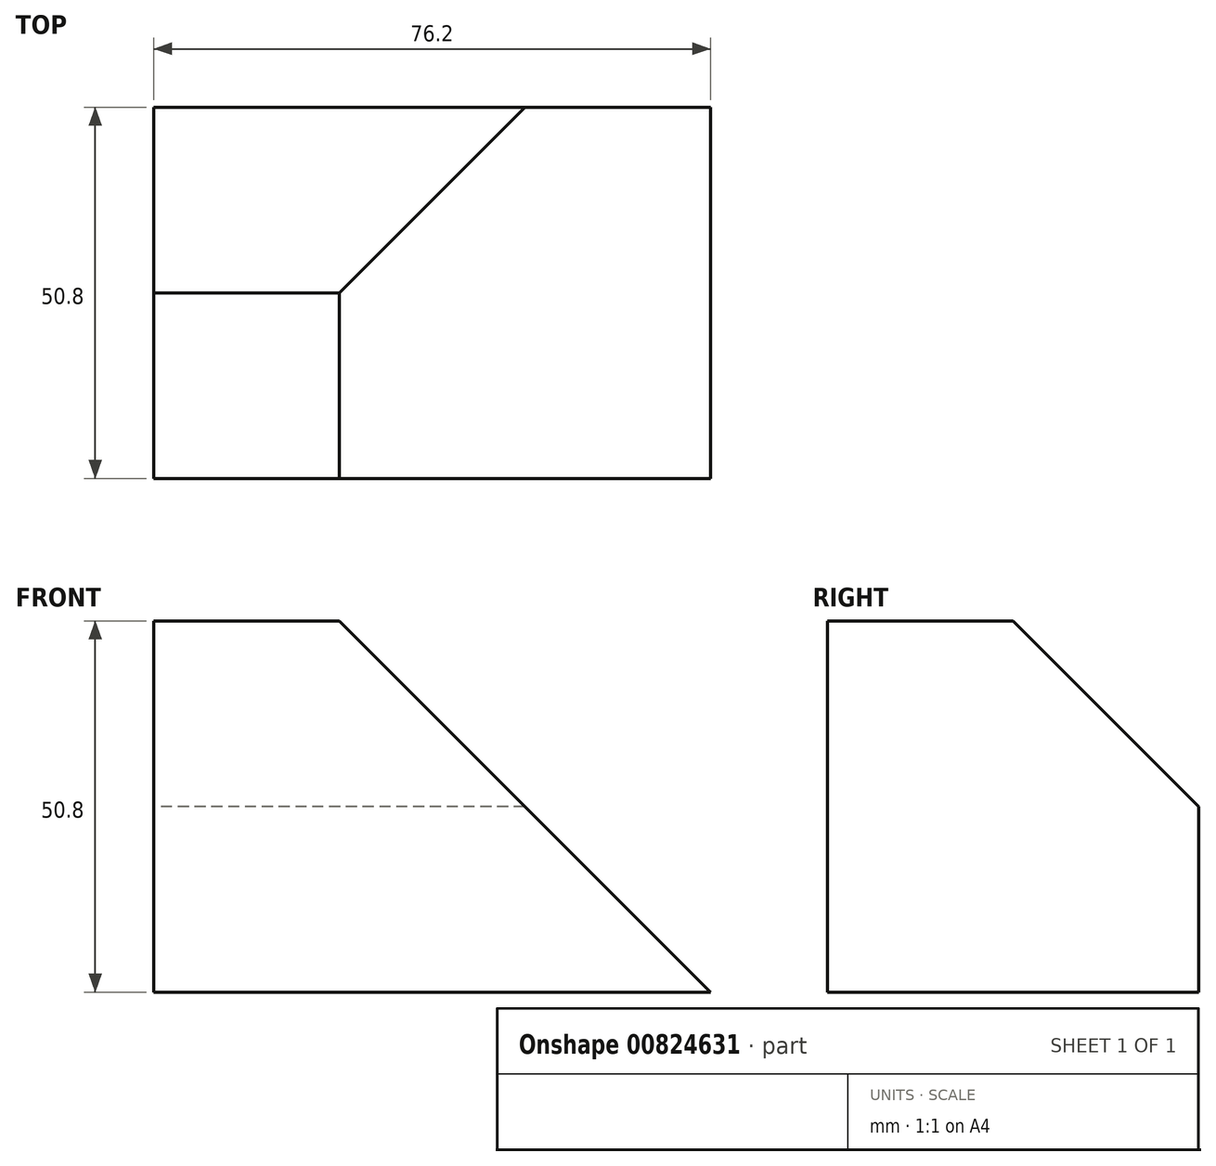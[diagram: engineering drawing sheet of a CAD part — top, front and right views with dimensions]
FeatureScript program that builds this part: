
annotation { "Feature Type Name" : "Feature", "Feature Type Description" : "" }
export const myFeature = defineFeature(function(context is Context, id is Id, definition is map)
    precondition{}
    {
        {
            var Q0;
            Q0=qCreatedBy(makeId("Front.planeOp"),FACE);
            var sketch = newSketch(context, id + "F0", { "sketchPlane" : qUnion([Q0])});
            skLineSegment(sketch, "E0", {"start": v(0, 0) * mm, "end": v(76.2, 0) * mm});
            skLineSegment(sketch, "E1", {"start": v(0, 0) * mm, "end": v(0, 25.4) * mm});
            skLineSegment(sketch, "E2", {"start": v(0, 25.4) * mm, "end": v(0, 50.8) * mm});
            skLineSegment(sketch, "E3", {"start": v(0, 50.8) * mm, "end": v(25.4, 50.8) * mm});
            skLineSegment(sketch, "E4", {"start": v(25.4, 50.8) * mm, "end": v(25.4, 25.4) * mm});
            skLineSegment(sketch, "E5", {"start": v(25.4, 25.4) * mm, "end": v(76.2, 0) * mm});
            skLineSegment(sketch, "E6", {"start": v(0, 25.4) * mm, "end": v(25.4, 25.4) * mm});
            skLineSegment(sketch, "E7", {"start": v(25.4, 50.8) * mm, "end": v(76.2, 0) * mm});
            skSolve(sketch);
        }
        {
            var Q0;
            Q0=makeQuery(id+"F0.imprint","IMPRINT",FACE,{"disambiguationData":[TD([[makeQuery(id+"F0.imprint","IMPRINT",EDGE,{"derivedFrom":sQuery(id+"F0.wireOp",EDGE,"E4")}),1.0]])]});
            var Q1;
            Q1=makeQuery(id+"F0.imprint","IMPRINT",FACE,{"disambiguationData":[TD([[makeQuery(id+"F0.imprint","IMPRINT",EDGE,{"derivedFrom":sQuery(id+"F0.wireOp",EDGE,"E2")}),-1.0]])]});
            var Q2;
            Q2=makeQuery(id+"F0.imprint","IMPRINT",FACE,{"disambiguationData":[TD([[makeQuery(id+"F0.imprint","IMPRINT",EDGE,{"derivedFrom":sQuery(id+"F0.wireOp",EDGE,"E0")}),1.0]])]});
            extrude(context, id + "F1", {"entities" : qUnion([Q0, Q1, Q2]), "depth" : 50.8 * mm, "offsetDistance" : 25.4 * mm});
        }
        {
            var Q0;
            Q0=makeQuery(id+"F1.opExtrude","SWEPT_FACE",FACE,{"disambiguationData":[OSD([sQuery(id+"F0.wireOp",EDGE,"E1"),sQuery(id+"F0.wireOp",EDGE,"E2")])]});
            var sketch = newSketch(context, id + "F2", { "sketchPlane" : qUnion([Q0])});
            skLineSegment(sketch, "E8", {"start": v(50.8, 0) * mm, "end": v(25.4, 0) * mm});
            skLineSegment(sketch, "E9", {"start": v(25.4, 0) * mm, "end": v(25.4, 50.8) * mm});
            skLineSegment(sketch, "E10", {"start": v(25.4, 50.8) * mm, "end": v(50.8, 50.8) * mm});
            skLineSegment(sketch, "E11", {"start": v(0, 0) * mm, "end": v(0, 25.4) * mm});
            skLineSegment(sketch, "E12", {"start": v(0, 25.4) * mm, "end": v(25.4, 50.8) * mm});
            skLineSegment(sketch, "E13", {"start": v(0, 25.4) * mm, "end": v(25.4, 25.4) * mm});
            skSolve(sketch);
        }
        {
            var Q0;
            {var subQ0=sQuery(id+"F2.wireOp",EDGE,"E12");Q0=makeQuery(id+"F2.imprint","IMPRINT",FACE,{"disambiguationData":[TD([[makeQuery(id+"F2.imprint","IMPRINT",EDGE,{"derivedFrom":subQ0}),1.0]])]});}
            extrude(context, id + "F3", {"entities" : qUnion([Q0]), "operationType" : NewBodyOperationType.REMOVE, "endBound" : BoundingType.THROUGH_ALL, "oppositeDirection" : true, "depth" : 25.4 * mm, "offsetDistance" : 25.4 * mm});
        }
    });
